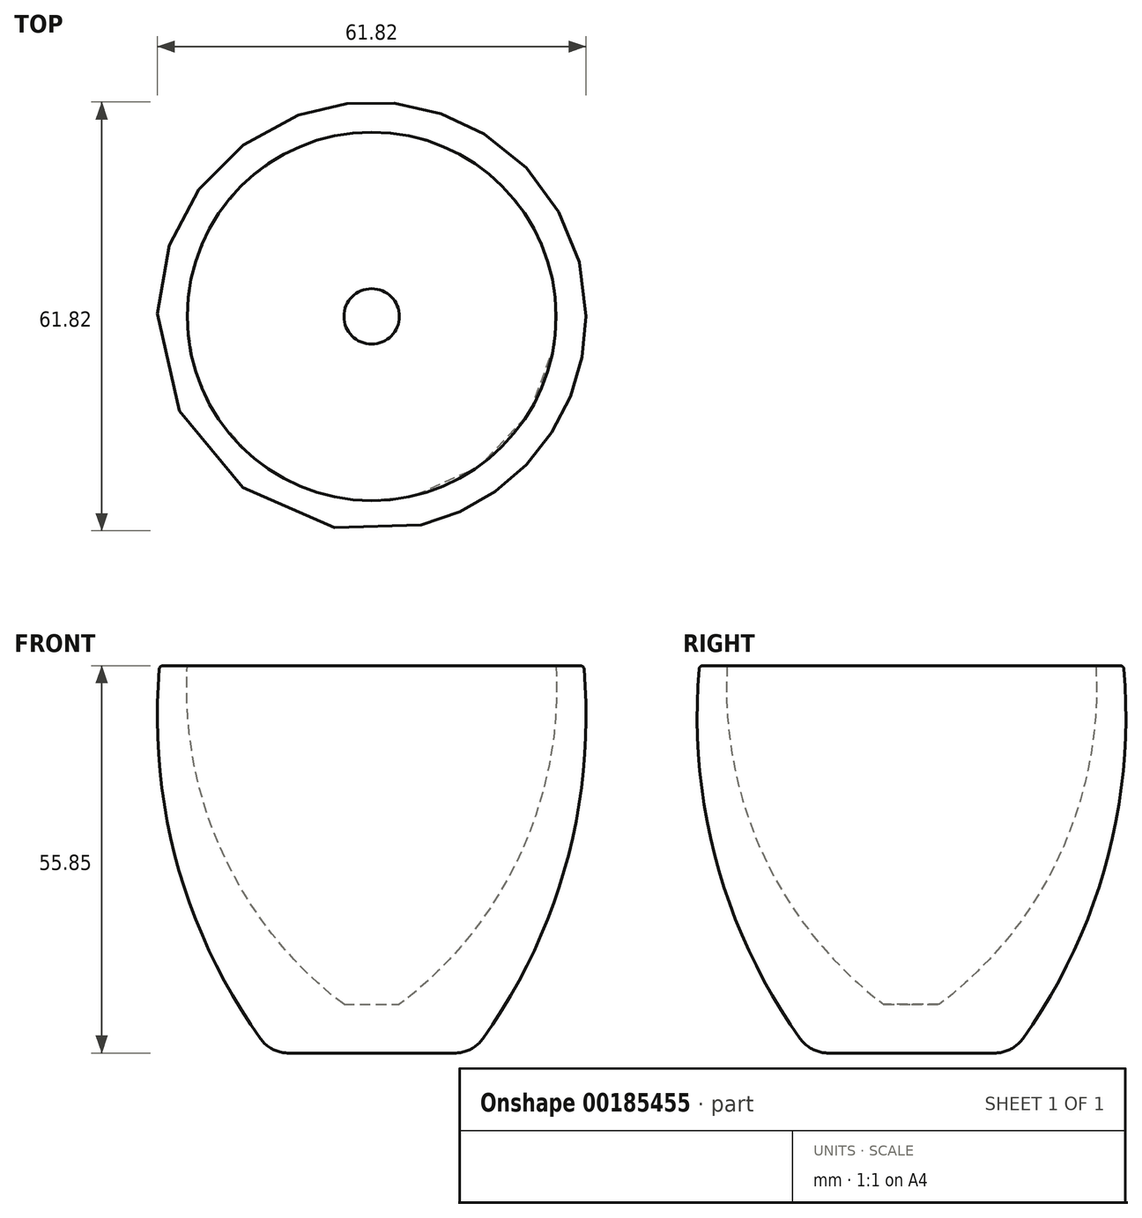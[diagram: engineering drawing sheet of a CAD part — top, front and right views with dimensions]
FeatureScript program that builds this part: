
annotation { "Feature Type Name" : "Feature", "Feature Type Description" : "" }
export const myFeature = defineFeature(function(context is Context, id is Id, definition is map)
    precondition{}
    {
        {
            var Q0;
            Q0=qCreatedBy(makeId("Front.planeOp"),FACE);
            var sketch = newSketch(context, id + "F0", { "sketchPlane" : qUnion([Q0])});
            skLineSegment(sketch, "E0", {"start": v(0, 0) * mm, "end": v(14.5, 0) * mm});
            skLineSegment(sketch, "E1", {"start": v(0, 0) * mm, "end": v(0, 7) * mm});
            skArc(sketch, "E2", {"start": v(14.5, 0) * mm, "mid": v(27.8, 26.42) * mm, "end": v(30.58, 55.85) * mm});
            skLineSegment(sketch, "E3", {"start": v(30.58, 55.85) * mm, "end": v(26.58, 55.85) * mm});
            skLineSegment(sketch, "E4", {"start": v(0, 7) * mm, "end": v(4, 7) * mm});
            skArc(sketch, "E5", {"start": v(4, 7) * mm, "mid": v(21.38, 28.61) * mm, "end": v(26.58, 55.85) * mm});
            skSolve(sketch);
        }
        {
            var Q0;
            Q0=makeQuery(id+"F0.imprint","IMPRINT",FACE,{"disambiguationData":[TD([[makeQuery(id+"F0.imprint","IMPRINT",EDGE,{"derivedFrom":sQuery(id+"F0.wireOp",EDGE,"E0")}),1.0]])]});
            var Q1;
            Q1=sQuery(id+"F0.wireOp",EDGE,"E1");
            revolve(context, id + "F1", {"entities" : qUnion([Q0]), "axis" : qUnion([Q1]), "revolveType" : RevolveType.FULL});
        }
        {
            var Q0;
            Q0=makeQuery(id+"F1.opRevolve","SWEPT_EDGE",EDGE,{"disambiguationData":[OSD([sQuery(id+"F0.wireOp",EDGE,"E0"),sQuery(id+"F0.wireOp",EDGE,"E2")])]});
            fillet(context, id + "F2", {"entities" : qUnion([Q0]), "radius" : 5 * mm, "tangentPropagation" : true, "allowEdgeOverflow" : false});
        }
        {
            var Q0;
            Q0=makeQuery(id+"F1.opRevolve","SWEPT_EDGE",EDGE,{"disambiguationData":[OSD([sQuery(id+"F0.wireOp",EDGE,"E2"),sQuery(id+"F0.wireOp",EDGE,"E3")])]});
            fillet(context, id + "F3", {"entities" : qUnion([Q0]), "radius" : 0.5 * mm, "tangentPropagation" : true, "allowEdgeOverflow" : false});
        }
    });
